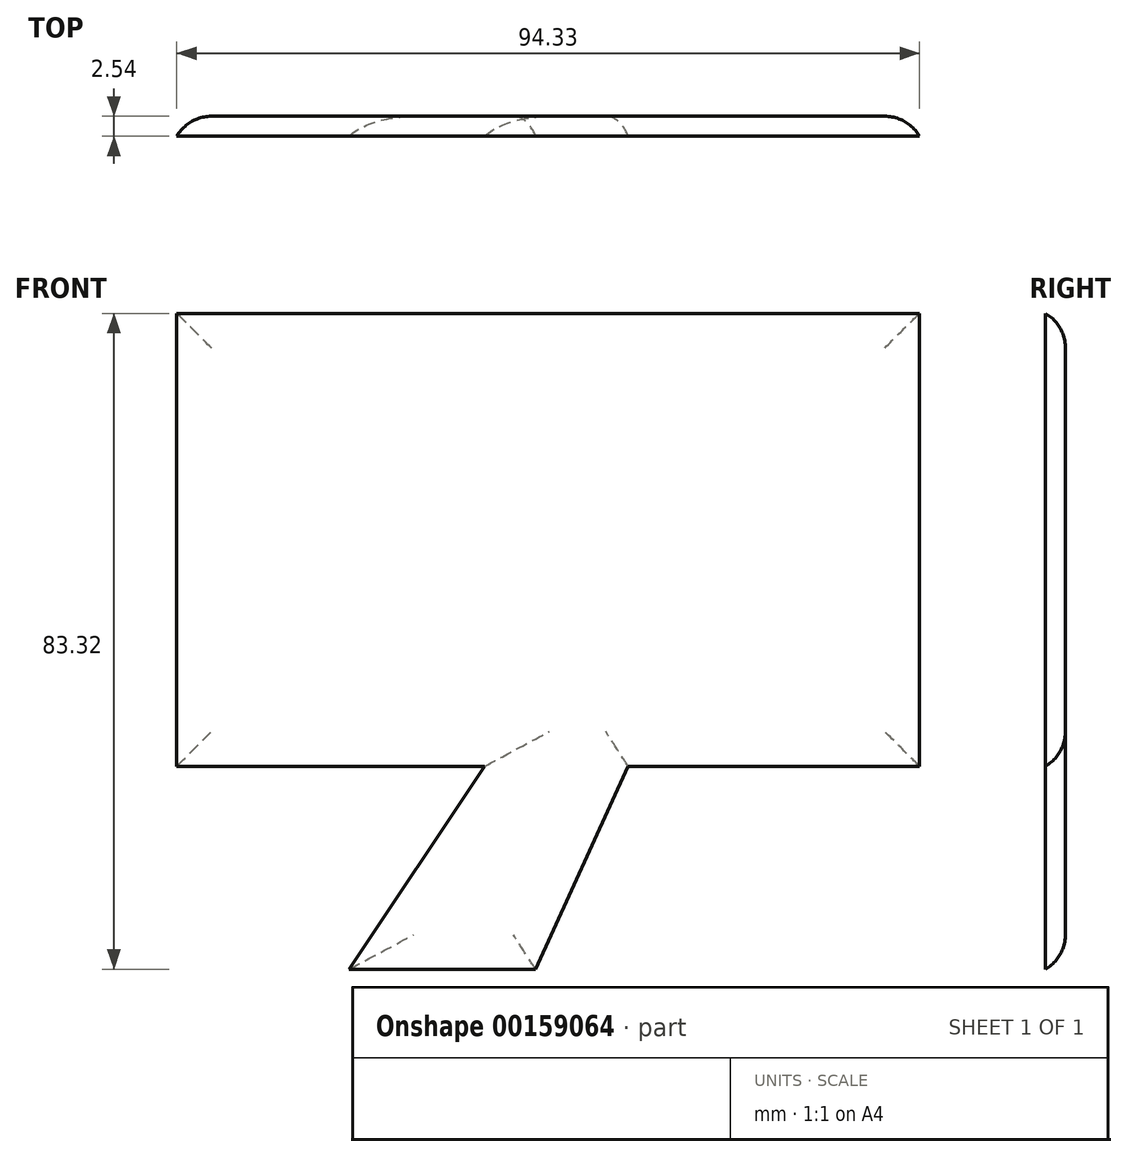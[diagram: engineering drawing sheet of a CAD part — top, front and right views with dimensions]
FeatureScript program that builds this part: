
annotation { "Feature Type Name" : "Feature", "Feature Type Description" : "" }
export const myFeature = defineFeature(function(context is Context, id is Id, definition is map)
    precondition{}
    {
        {
            var Q0;
            Q0=qCreatedBy(makeId("Front.planeOp"),FACE);
            var sketch = newSketch(context, id + "F0", { "sketchPlane" : qUnion([Q0])});
            skLineSegment(sketch, "E0.bottom", {"start": v(-26.47, 19.11) * mm, "end": v(67.86, 19.11) * mm});
            skLineSegment(sketch, "E0.top", {"start": v(-26.47, -38.42) * mm, "end": v(67.86, -38.42) * mm});
            skLineSegment(sketch, "E0.left", {"start": v(-26.47, 19.11) * mm, "end": v(-26.47, -38.42) * mm});
            skLineSegment(sketch, "E0.right", {"start": v(67.86, 19.11) * mm, "end": v(67.86, -38.42) * mm});
            skLineSegment(sketch, "E1", {"start": v(12.63, -38.42) * mm, "end": v(-4.6, -64.21) * mm});
            skLineSegment(sketch, "E2", {"start": v(-4.6, -64.21) * mm, "end": v(19.1, -64.21) * mm});
            skLineSegment(sketch, "E3", {"start": v(19.1, -64.21) * mm, "end": v(30.85, -38.42) * mm});
            skSolve(sketch);
        }
        {
            var Q0;
            Q0 = qSketchRegion(id + "F0", true);
            extrude(context, id + "F1", {"entities" : qUnion([Q0]), "depth" : 2.54 * mm});
        }
        {
            var Q0;
            Q0=makeQuery(id+"F1.opExtrude","CAP_EDGE",EDGE,{"disambiguationData":[OSD([sQuery(id+"F0.wireOp",EDGE,"E0.bottom")])],"isStart":true});
            var Q1;
            {var subQ0=sQuery(id+"F0.wireOp",EDGE,"E0.top");Q1=makeQuery(id+"F1.opExtrude","CAP_EDGE",EDGE,{"disambiguationData":[OSD([subQ0]),TDD([makeQuery(id+"F0.imprint","IMPRINT",EDGE,{"disambiguationData":[TD([[makeQuery(id+"F0.imprint","INTERSECT",VERTEX,{"derivedFrom":[subQ0,sQuery(id+"F0.wireOp",EDGE,"E0.left")]}),-1.0]])],"derivedFrom":subQ0})])],"isStart":true});}
            var Q2;
            Q2=makeQuery(id+"F1.opExtrude","CAP_FACE",FACE,{"disambiguationData":[OSD([sQuery(id+"F0.wireOp",EDGE,"E0.bottom"),sQuery(id+"F0.wireOp",EDGE,"E0.top"),sQuery(id+"F0.wireOp",EDGE,"E0.left"),sQuery(id+"F0.wireOp",EDGE,"E0.right"),sQuery(id+"F0.wireOp",EDGE,"E1"),sQuery(id+"F0.wireOp",EDGE,"E2"),sQuery(id+"F0.wireOp",EDGE,"E3")])],"isStart":true});
            fillet(context, id + "F2", {"entities" : qUnion([Q0, Q1, Q2]), "radius" : 5.08 * mm, "tangentPropagation" : true, "allowEdgeOverflow" : false});
        }
    });
